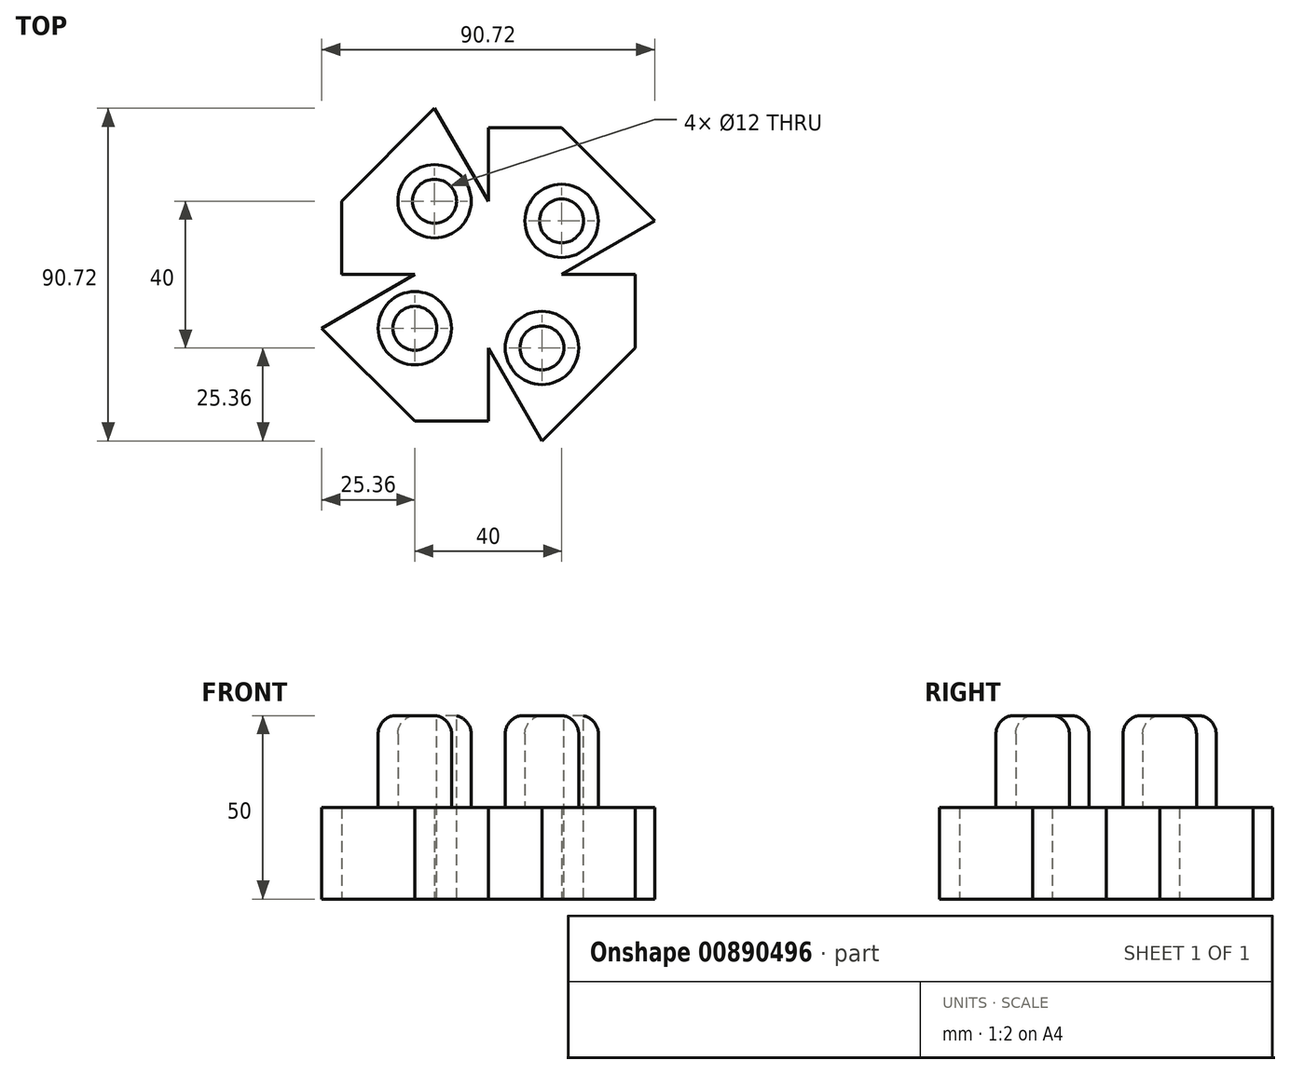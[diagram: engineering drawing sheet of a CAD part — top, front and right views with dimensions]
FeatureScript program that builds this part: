
annotation { "Feature Type Name" : "Feature", "Feature Type Description" : "" }
export const myFeature = defineFeature(function(context is Context, id is Id, definition is map)
    precondition{}
    {
        {
            var Q0;
            Q0=qCreatedBy(makeId("Top.planeOp"),FACE);
            var sketch = newSketch(context, id + "F0", { "sketchPlane" : qUnion([Q0])});
            skLineSegment(sketch, "E0", {"start": v(0, 0) * mm, "end": v(-40, 0) * mm});
            skLineSegment(sketch, "E1", {"start": v(-40, 0) * mm, "end": v(-40, 20) * mm});
            skLineSegment(sketch, "E2", {"start": v(-40, 20) * mm, "end": v(0, 20) * mm, "construction": true});
            skLineSegment(sketch, "E3", {"start": v(0, 20) * mm, "end": v(0, 0) * mm});
            skLineSegment(sketch, "E4", {"start": v(-40, 20) * mm, "end": v(-14.64, 45.36) * mm});
            skLineSegment(sketch, "E5", {"start": v(0, 20) * mm, "end": v(-14.64, 45.36) * mm});
            skLineSegment(sketch, "E6", {"start": v(-14.64, 45.36) * mm, "end": v(-14.64, 0) * mm, "construction": true});
            skCircle(sketch, "E7", {"center": v(-14.64, 20) * mm, "radius": 10 * mm});
            skArc(sketch, "E8", {"start": v(-17.22, 29.66) * mm, "mid": v(-33.65, 18.7) * mm, "end": v(-40, 0) * mm});
            skLineSegment(sketch, "E9", {"start": v(0, 0) * mm, "end": v(0, 57.81) * mm, "construction": true});
            skLineSegment(sketch, "E10.1.0", {"start": v(-20, -40) * mm, "end": v(-45.36, -14.64) * mm});
            skCircle(sketch, "E10.1.1", {"center": v(-20, -14.64) * mm, "radius": 10 * mm});
            skLineSegment(sketch, "E10.1.2", {"start": v(-20, -40) * mm, "end": v(-20, 0) * mm, "construction": true});
            skLineSegment(sketch, "E10.1.3", {"start": v(0, -40) * mm, "end": v(-20, -40) * mm});
            skArc(sketch, "E10.1.4", {"start": v(-29.66, -17.22) * mm, "mid": v(-18.7, -33.65) * mm, "end": v(0, -40) * mm});
            skLineSegment(sketch, "E10.1.5", {"start": v(0, 0) * mm, "end": v(0, -40) * mm});
            skLineSegment(sketch, "E10.1.6", {"start": v(-20, 0) * mm, "end": v(-45.36, -14.64) * mm});
            skLineSegment(sketch, "E10.1.7", {"start": v(-45.36, -14.64) * mm, "end": v(0, -14.64) * mm, "construction": true});
            skLineSegment(sketch, "E10.1.8", {"start": v(-20, 0) * mm, "end": v(0, 0) * mm});
            skLineSegment(sketch, "E10.2.0", {"start": v(40, -20) * mm, "end": v(14.64, -45.36) * mm});
            skCircle(sketch, "E10.2.1", {"center": v(14.64, -20) * mm, "radius": 10 * mm});
            skLineSegment(sketch, "E10.2.2", {"start": v(40, -20) * mm, "end": v(0, -20) * mm, "construction": true});
            skLineSegment(sketch, "E10.2.3", {"start": v(40, 0) * mm, "end": v(40, -20) * mm});
            skArc(sketch, "E10.2.4", {"start": v(17.22, -29.66) * mm, "mid": v(33.65, -18.7) * mm, "end": v(40, 0) * mm});
            skLineSegment(sketch, "E10.2.5", {"start": v(0, 0) * mm, "end": v(40, 0) * mm});
            skLineSegment(sketch, "E10.2.6", {"start": v(0, -20) * mm, "end": v(14.64, -45.36) * mm});
            skLineSegment(sketch, "E10.2.7", {"start": v(14.64, -45.36) * mm, "end": v(14.64, 0) * mm, "construction": true});
            skLineSegment(sketch, "E10.2.8", {"start": v(0, -20) * mm, "end": v(0, 0) * mm});
            skPoint(sketch, "E10.center", {"position": v(0, 0) * mm});
            skCircle(sketch, "E11.3.3.0", {"center": v(20, 14.64) * mm, "radius": 10 * mm});
            skLineSegment(sketch, "E11.5.3.0", {"start": v(20, 40) * mm, "end": v(20, 0) * mm, "construction": true});
            skLineSegment(sketch, "E11.8.3.0", {"start": v(0, 40) * mm, "end": v(20, 40) * mm});
            skLineSegment(sketch, "E11.9.3.0", {"start": v(20, 40) * mm, "end": v(45.36, 14.64) * mm});
            skArc(sketch, "E11.11.3.0", {"start": v(29.66, 17.22) * mm, "mid": v(18.7, 33.65) * mm, "end": v(0, 40) * mm});
            skLineSegment(sketch, "E11.15.3.0", {"start": v(0, 0) * mm, "end": v(0, 40) * mm});
            skLineSegment(sketch, "E11.18.3.0", {"start": v(20, 0) * mm, "end": v(45.36, 14.64) * mm});
            skLineSegment(sketch, "E11.21.3.0", {"start": v(45.36, 14.64) * mm, "end": v(0, 14.64) * mm, "construction": true});
            skLineSegment(sketch, "E11.24.3.0", {"start": v(20, 0) * mm, "end": v(0, 0) * mm});
            skSolve(sketch);
        }
        {
            var Q0;
            Q0=makeQuery(id+"F0.imprint","IMPRINT",FACE,{"disambiguationData":[TD([[makeQuery(id+"F0.imprint","IMPRINT",EDGE,{"derivedFrom":sQuery(id+"F0.wireOp",EDGE,"E10.1.1")}),1.0]])]});
            var Q1;
            Q1=makeQuery(id+"F0.imprint","IMPRINT",FACE,{"disambiguationData":[TD([[makeQuery(id+"F0.imprint","IMPRINT",EDGE,{"derivedFrom":sQuery(id+"F0.wireOp",EDGE,"E10.1.0")}),-1.0]])]});
            var Q2;
            Q2=makeQuery(id+"F0.imprint","IMPRINT",FACE,{"disambiguationData":[TD([[makeQuery(id+"F0.imprint","IMPRINT",EDGE,{"derivedFrom":sQuery(id+"F0.wireOp",EDGE,"E0")}),-1.0]])]});
            var Q3;
            Q3=makeQuery(id+"F0.imprint","IMPRINT",FACE,{"disambiguationData":[TD([[makeQuery(id+"F0.imprint","IMPRINT",EDGE,{"derivedFrom":sQuery(id+"F0.wireOp",EDGE,"E7")}),1.0]])]});
            var Q4;
            Q4=makeQuery(id+"F0.imprint","IMPRINT",FACE,{"disambiguationData":[TD([[makeQuery(id+"F0.imprint","IMPRINT",EDGE,{"derivedFrom":sQuery(id+"F0.wireOp",EDGE,"E11.3.3.0")}),-1.0]])]});
            var Q5;
            Q5=makeQuery(id+"F0.imprint","IMPRINT",FACE,{"disambiguationData":[TD([[makeQuery(id+"F0.imprint","IMPRINT",EDGE,{"derivedFrom":sQuery(id+"F0.wireOp",EDGE,"E11.3.3.0")}),1.0]])]});
            var Q6;
            Q6=makeQuery(id+"F0.imprint","IMPRINT",FACE,{"disambiguationData":[TD([[makeQuery(id+"F0.imprint","IMPRINT",EDGE,{"derivedFrom":sQuery(id+"F0.wireOp",EDGE,"E10.2.1")}),1.0]])]});
            var Q7;
            Q7=makeQuery(id+"F0.imprint","IMPRINT",FACE,{"disambiguationData":[TD([[makeQuery(id+"F0.imprint","IMPRINT",EDGE,{"derivedFrom":sQuery(id+"F0.wireOp",EDGE,"E10.2.0")}),-1.0]])]});
            extrude(context, id + "F1", {"entities" : qUnion([Q0, Q1, Q2, Q3, Q4, Q5, Q6, Q7]), "depth" : 25 * mm, "offsetDistance" : 25 * mm});
        }
        {
            var Q0;
            Q0=makeQuery(id+"F0.imprint","IMPRINT",FACE,{"disambiguationData":[TD([[makeQuery(id+"F0.imprint","IMPRINT",EDGE,{"derivedFrom":sQuery(id+"F0.wireOp",EDGE,"E10.2.1")}),1.0]])]});
            var Q1;
            Q1=makeQuery(id+"F0.imprint","IMPRINT",FACE,{"disambiguationData":[TD([[makeQuery(id+"F0.imprint","IMPRINT",EDGE,{"derivedFrom":sQuery(id+"F0.wireOp",EDGE,"E10.1.1")}),1.0]])]});
            var Q2;
            Q2=makeQuery(id+"F0.imprint","IMPRINT",FACE,{"disambiguationData":[TD([[makeQuery(id+"F0.imprint","IMPRINT",EDGE,{"derivedFrom":sQuery(id+"F0.wireOp",EDGE,"E7")}),1.0]])]});
            var Q3;
            Q3=makeQuery(id+"F0.imprint","IMPRINT",FACE,{"disambiguationData":[TD([[makeQuery(id+"F0.imprint","IMPRINT",EDGE,{"derivedFrom":sQuery(id+"F0.wireOp",EDGE,"E11.3.3.0")}),1.0]])]});
            extrude(context, id + "F2", {"entities" : qUnion([Q0, Q1, Q2, Q3]), "operationType" : NewBodyOperationType.ADD, "depth" : 50 * mm, "offsetDistance" : 25 * mm});
        }
        {
            var Q0;
            Q0=makeQuery(id+"F2.opExtrude","CAP_FACE",FACE,{"disambiguationData":[OSD([sQuery(id+"F0.wireOp",EDGE,"E10.1.1")])],"isStart":false});
            var sketch = newSketch(context, id + "F3", { "sketchPlane" : qUnion([Q0])});
            skCircle(sketch, "E12", {"center": v(-14.64, 20) * mm, "radius": 6 * mm});
            skCircle(sketch, "E13", {"center": v(20, 14.64) * mm, "radius": 6 * mm});
            skCircle(sketch, "E14", {"center": v(14.64, -20) * mm, "radius": 6 * mm});
            skCircle(sketch, "E15", {"center": v(-20, -14.64) * mm, "radius": 6 * mm});
            skSolve(sketch);
        }
        {
            var Q0;
            Q0=makeQuery(id+"F3.imprint","IMPRINT",FACE,{"disambiguationData":[TD([[makeQuery(id+"F3.imprint","IMPRINT",EDGE,{"derivedFrom":sQuery(id+"F3.wireOp",EDGE,"E12")}),1.0]])]});
            extrude(context, id + "F4", {"entities" : qUnion([Q0]), "operationType" : NewBodyOperationType.REMOVE, "oppositeDirection" : true, "depth" : 50 * mm, "offsetDistance" : 25 * mm});
        }
        {
            var Q0;
            Q0=makeQuery(id+"F3.imprint","IMPRINT",FACE,{"disambiguationData":[TD([[makeQuery(id+"F3.imprint","IMPRINT",EDGE,{"derivedFrom":sQuery(id+"F3.wireOp",EDGE,"E13")}),1.0]])]});
            var Q1;
            Q1=makeQuery(id+"F3.imprint","IMPRINT",FACE,{"disambiguationData":[TD([[makeQuery(id+"F3.imprint","IMPRINT",EDGE,{"derivedFrom":sQuery(id+"F3.wireOp",EDGE,"E14")}),1.0]])]});
            var Q2;
            Q2=makeQuery(id+"F3.imprint","IMPRINT",FACE,{"disambiguationData":[TD([[makeQuery(id+"F3.imprint","IMPRINT",EDGE,{"derivedFrom":sQuery(id+"F3.wireOp",EDGE,"E15")}),1.0]])]});
            var Q3;
            Q3=makeQuery(id+"F3.imprint","IMPRINT",FACE,{"disambiguationData":[TD([[makeQuery(id+"F3.imprint","IMPRINT",EDGE,{"derivedFrom":sQuery(id+"F3.wireOp",EDGE,"E12")}),1.0]])]});
            extrude(context, id + "F5", {"entities" : qUnion([Q0, Q1, Q2, Q3]), "operationType" : NewBodyOperationType.REMOVE, "oppositeDirection" : true, "depth" : 50 * mm, "offsetDistance" : 25 * mm});
        }
        {
            var Q0;
            Q0=makeQuery(id+"F2.opExtrude","CAP_EDGE",EDGE,{"disambiguationData":[OSD([sQuery(id+"F0.wireOp",EDGE,"E10.1.1")])],"isStart":false});
            var Q1;
            Q1=makeQuery(id+"F2.opExtrude","CAP_EDGE",EDGE,{"disambiguationData":[OSD([sQuery(id+"F0.wireOp",EDGE,"E7")])],"isStart":false});
            var Q2;
            Q2=makeQuery(id+"F2.opExtrude","CAP_EDGE",EDGE,{"disambiguationData":[OSD([sQuery(id+"F0.wireOp",EDGE,"E10.2.1")])],"isStart":false});
            var Q3;
            Q3=makeQuery(id+"F2.opExtrude","CAP_EDGE",EDGE,{"disambiguationData":[OSD([sQuery(id+"F0.wireOp",EDGE,"E11.3.3.0")])],"isStart":false});
            fillet(context, id + "F6", {"entities" : qUnion([Q0, Q1, Q2, Q3]), "radius" : 5 * mm, "tangentPropagation" : true, "allowEdgeOverflow" : false});
        }
    });
